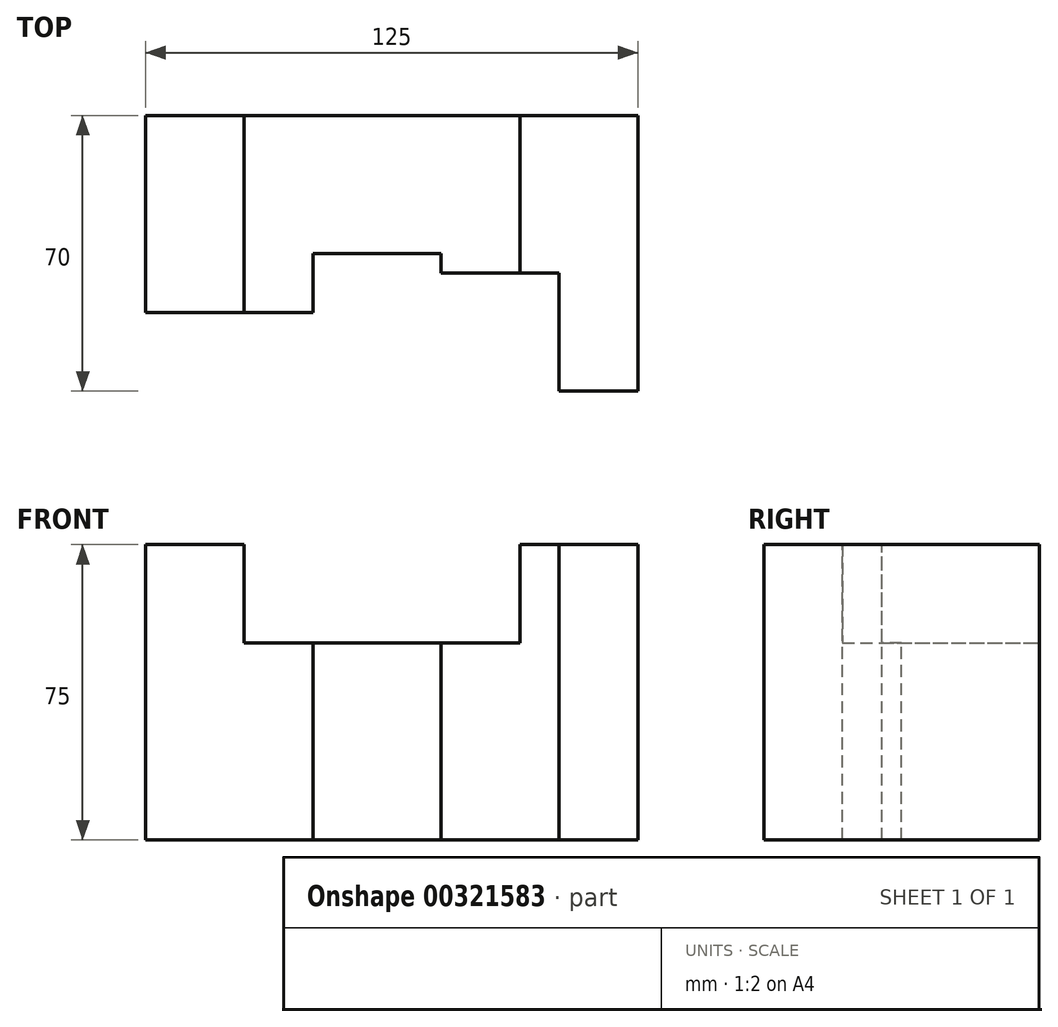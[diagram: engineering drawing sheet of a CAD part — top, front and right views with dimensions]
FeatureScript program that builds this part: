
annotation { "Feature Type Name" : "Feature", "Feature Type Description" : "" }
export const myFeature = defineFeature(function(context is Context, id is Id, definition is map)
    precondition{}
    {
        {
            var Q0;
            Q0=qCreatedBy(makeId("Front.planeOp"),FACE);
            var sketch = newSketch(context, id + "F0", { "sketchPlane" : qUnion([Q0])});
            skLineSegment(sketch, "E0", {"start": v(0, 0) * mm, "end": v(0, 75) * mm});
            skLineSegment(sketch, "E1", {"start": v(0, 75) * mm, "end": v(25, 75) * mm});
            skLineSegment(sketch, "E2", {"start": v(25, 75) * mm, "end": v(25, 50) * mm});
            skLineSegment(sketch, "E3", {"start": v(25, 50) * mm, "end": v(95, 50) * mm});
            skLineSegment(sketch, "E4", {"start": v(95, 50) * mm, "end": v(95, 75) * mm});
            skLineSegment(sketch, "E5", {"start": v(95, 75) * mm, "end": v(125, 75) * mm});
            skLineSegment(sketch, "E6", {"start": v(125, 75) * mm, "end": v(125, 0) * mm});
            skLineSegment(sketch, "E7", {"start": v(125, 0) * mm, "end": v(0, 0) * mm});
            skSolve(sketch);
        }
        {
            var Q0;
            Q0=makeQuery(id+"F0.imprint","IMPRINT",FACE,{"disambiguationData":[TD([[makeQuery(id+"F0.imprint","IMPRINT",EDGE,{"derivedFrom":sQuery(id+"F0.wireOp",EDGE,"E0")}),-1.0]])]});
            extrude(context, id + "F1", {"entities" : qUnion([Q0]), "depth" : 50 * mm});
        }
        {
            var Q0;
            Q0=makeQuery(id+"F1.opExtrude","SWEPT_FACE",FACE,{"disambiguationData":[OSD([sQuery(id+"F0.wireOp",EDGE,"E3")])]});
            var sketch = newSketch(context, id + "F2", { "sketchPlane" : qUnion([Q0])});
            skLineSegment(sketch, "E8.0.0", {"start": v(95, 0) * mm, "end": v(25, 0) * mm});
            skLineSegment(sketch, "E8.0.1", {"start": v(25, 0) * mm, "end": v(25, -50) * mm});
            skLineSegment(sketch, "E8.0.2", {"start": v(25, -50) * mm, "end": v(95, -50) * mm});
            skLineSegment(sketch, "E8.0.3", {"start": v(95, -50) * mm, "end": v(95, 0) * mm});
            skLineSegment(sketch, "E9", {"start": v(25, -50) * mm, "end": v(42.5, -50) * mm});
            skLineSegment(sketch, "E10", {"start": v(42.5, -50) * mm, "end": v(42.5, -35) * mm});
            skLineSegment(sketch, "E11", {"start": v(42.5, -35) * mm, "end": v(75, -35) * mm});
            skLineSegment(sketch, "E12", {"start": v(75, -35) * mm, "end": v(75, -40) * mm});
            skLineSegment(sketch, "E13", {"start": v(75, -40) * mm, "end": v(95, -40) * mm});
            skLineSegment(sketch, "E14", {"start": v(95, -40) * mm, "end": v(95, -50) * mm});
            skSolve(sketch);
        }
        {
            var Q0;
            Q0=makeQuery(id+"F2.imprint","IMPRINT",FACE,{"disambiguationData":[TD([[makeQuery(id+"F2.imprint","IMPRINT",EDGE,{"derivedFrom":sQuery(id+"F2.wireOp",EDGE,"E8.0.2")}),1.0]])]});
            extrude(context, id + "F3", {"entities" : qUnion([Q0]), "operationType" : NewBodyOperationType.REMOVE, "endBound" : BoundingType.THROUGH_ALL, "oppositeDirection" : true, "depth" : 25 * mm});
        }
        {
            var Q0;
            Q0=makeQuery(id+"F1.opExtrude","SWEPT_FACE",FACE,{"disambiguationData":[OSD([sQuery(id+"F0.wireOp",EDGE,"E5")])]});
            var sketch = newSketch(context, id + "F4", { "sketchPlane" : qUnion([Q0])});
            skLineSegment(sketch, "E15", {"start": v(95, -50) * mm, "end": v(95, -70) * mm});
            skLineSegment(sketch, "E16", {"start": v(95, -70) * mm, "end": v(125, -70) * mm});
            skLineSegment(sketch, "E17", {"start": v(125, -70) * mm, "end": v(125, -50) * mm});
            skLineSegment(sketch, "E18", {"start": v(125, -50) * mm, "end": v(95, -50) * mm});
            skSolve(sketch);
        }
        {
            var Q0;
            Q0 = qSketchRegion(id + "F4", true);
            extrude(context, id + "F5", {"entities" : qUnion([Q0]), "operationType" : NewBodyOperationType.ADD, "oppositeDirection" : true, "depth" : 75 * mm});
        }
        {
            var Q0;
            Q0=makeQuery(id+"F5.boolean.opBoolean","MERGE",FACE,{"derivedFrom":[makeQuery(id+"F1.opExtrude","SWEPT_FACE",FACE,{"disambiguationData":[OSD([sQuery(id+"F0.wireOp",EDGE,"E5")])]}),makeQuery(id+"F5.opExtrude","CAP_FACE",FACE,{"disambiguationData":[OSD([sQuery(id+"F4.wireOp",EDGE,"E15"),sQuery(id+"F4.wireOp",EDGE,"E16"),sQuery(id+"F4.wireOp",EDGE,"E17"),sQuery(id+"F4.wireOp",EDGE,"E18")])],"isStart":true})]});
            var sketch = newSketch(context, id + "F6", { "sketchPlane" : qUnion([Q0])});
            skLineSegment(sketch, "E19", {"start": v(95, -70) * mm, "end": v(105, -70) * mm});
            skLineSegment(sketch, "E20", {"start": v(105, -70) * mm, "end": v(105, -40) * mm});
            skLineSegment(sketch, "E21", {"start": v(105, -40) * mm, "end": v(95, -40) * mm});
            skLineSegment(sketch, "E22", {"start": v(95, -40) * mm, "end": v(95, -70) * mm});
            skSolve(sketch);
        }
        {
            var Q0;
            Q0=makeQuery(id+"F6.imprint","IMPRINT",FACE,{"disambiguationData":[TD([[makeQuery(id+"F6.imprint","IMPRINT",EDGE,{"derivedFrom":sQuery(id+"F6.wireOp",EDGE,"E19")}),1.0]])]});
            extrude(context, id + "F7", {"entities" : qUnion([Q0]), "operationType" : NewBodyOperationType.REMOVE, "endBound" : BoundingType.THROUGH_ALL, "oppositeDirection" : true, "depth" : 25 * mm});
        }
    });
